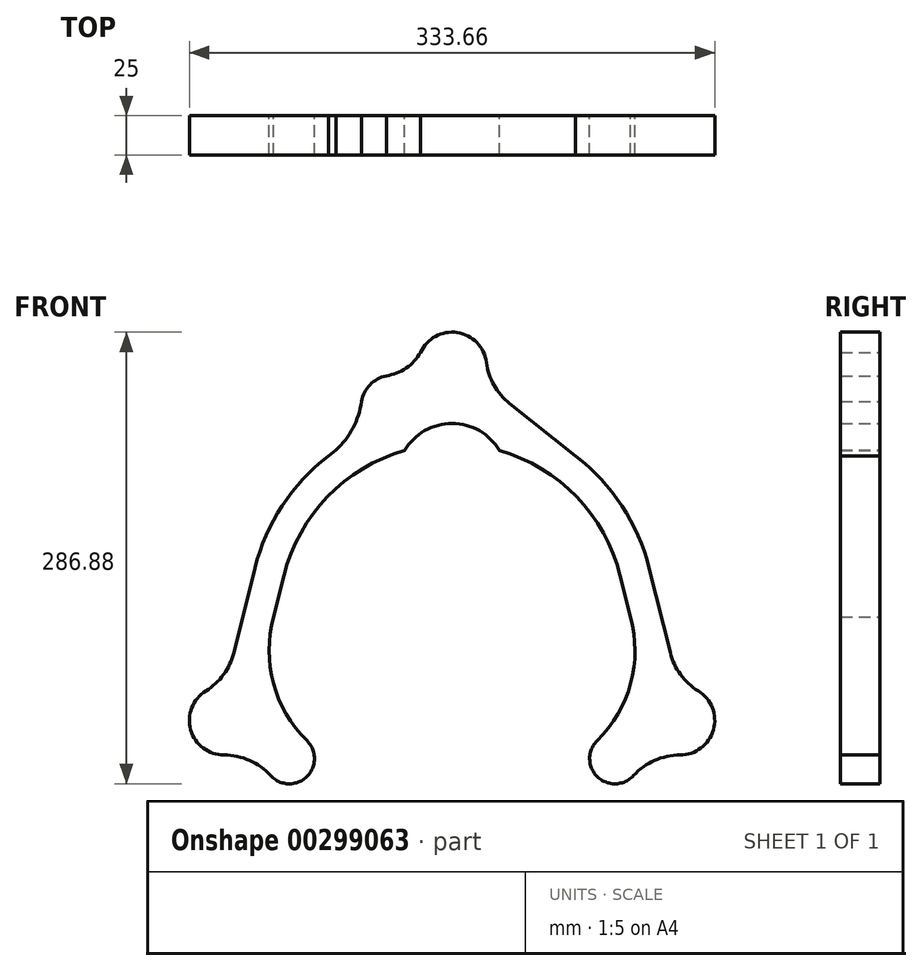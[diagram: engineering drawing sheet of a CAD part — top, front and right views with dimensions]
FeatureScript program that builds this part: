
annotation { "Feature Type Name" : "Feature", "Feature Type Description" : "" }
export const myFeature = defineFeature(function(context is Context, id is Id, definition is map)
    precondition{}
    {
        {
            var Q0;
            Q0=qCreatedBy(makeId("Front.planeOp"),FACE);
            var sketch = newSketch(context, id + "F0", { "sketchPlane" : qUnion([Q0])});
            skPoint(sketch, "E0", {"position": v(0, 88) * mm});
            skArc(sketch, "E1", {"start": v(30.14, 105.79) * mm, "mid": v(17.35, 118.4) * mm, "end": v(0, 123) * mm});
            skLineSegment(sketch, "E2", {"start": v(106.73, 26.61) * mm, "end": v(125.17, 31.2) * mm});
            skLineSegment(sketch, "E3", {"start": v(106.73, 26.61) * mm, "end": v(113.37, 0) * mm});
            skLineSegment(sketch, "E4", {"start": v(113.28, 0) * mm, "end": v(132.95, 0) * mm});
            skArc(sketch, "E5.trimOffspring", {"start": v(106.73, 26.61) * mm, "mid": v(79.06, 76.48) * mm, "end": v(30.14, 105.79) * mm});
            skPoint(sketch, "E6", {"position": v(103.4, -89.88) * mm});
            skArc(sketch, "E7", {"start": v(92.2, -78.45) * mm, "mid": v(92.3, -101.4) * mm, "end": v(115.22, -100.66) * mm});
            skLineSegment(sketch, "E8.trimOffspring", {"start": v(76.29, -181.97) * mm, "end": v(78.18, -189.55) * mm});
            skArc(sketch, "E9.trimOffspring", {"start": v(92.2, -78.45) * mm, "mid": v(113.45, -42.1) * mm, "end": v(113.28, 0) * mm});
            skPoint(sketch, "E10", {"position": v(144.83, -65.62) * mm});
            skArc(sketch, "E11", {"start": v(144.8, -87.62) * mm, "mid": v(166, -71.63) * mm, "end": v(156.38, -46.9) * mm});
            skArc(sketch, "E12.trimOffspring", {"start": v(144.8, -87.62) * mm, "mid": v(128.64, -91.02) * mm, "end": v(115.22, -100.66) * mm});
            skLineSegment(sketch, "E13.0", {"start": v(125.17, 31.2) * mm, "end": v(131.8, 4.6) * mm});
            skLineSegment(sketch, "E14", {"start": v(131.8, 4.6) * mm, "end": v(138.57, -22.53) * mm});
            skArc(sketch, "E15.trimOffspring", {"start": v(138.57, -22.53) * mm, "mid": v(145.09, -36.46) * mm, "end": v(156.38, -46.9) * mm});
            skArc(sketch, "E16.0", {"start": v(125.17, 31.2) * mm, "mid": v(107.88, 70.73) * mm, "end": v(78.53, 102.34) * mm});
            skLineSegment(sketch, "E17", {"start": v(78.53, 102.34) * mm, "end": v(36.58, 135.71) * mm});
            skArc(sketch, "E18", {"start": v(21.82, 161.84) * mm, "mid": v(14.52, 175.53) * mm, "end": v(0, 181) * mm});
            skLineSegment(sketch, "E19.0", {"start": v(103.43, 133.65) * mm, "end": v(102.88, 134.08) * mm});
            skArc(sketch, "E20", {"start": v(21.82, 161.84) * mm, "mid": v(26.65, 147.34) * mm, "end": v(36.58, 135.71) * mm});
            skPoint(sketch, "E21", {"position": v(-37.77, 127.52) * mm});
            skPoint(sketch, "E22", {"position": v(-37.77, 133.59) * mm});
            skArc(sketch, "E23", {"start": v(-41.75, 153.26) * mm, "mid": v(-52.18, 147.56) * mm, "end": v(-57.55, 136.96) * mm});
            skLineSegment(sketch, "E24.MirrorCS", {"start": v(-103.43, 133.65) * mm, "end": v(-102.88, 134.08) * mm});
            skLineSegment(sketch, "E25.MirrorCS", {"start": v(-78.53, 102.34) * mm, "end": v(-69.5, 109.52) * mm});
            skArc(sketch, "E26.MirrorCS", {"start": v(-144.8, -87.62) * mm, "mid": v(-166, -71.63) * mm, "end": v(-156.38, -46.9) * mm});
            skArc(sketch, "E27.MirrorCS", {"start": v(-92.2, -78.45) * mm, "mid": v(-92.3, -101.4) * mm, "end": v(-115.22, -100.66) * mm});
            skArc(sketch, "E28.MirrorCS", {"start": v(-138.57, -22.53) * mm, "mid": v(-145.09, -36.46) * mm, "end": v(-156.38, -46.9) * mm});
            skArc(sketch, "E29.MirrorCS", {"start": v(-144.8, -87.62) * mm, "mid": v(-128.64, -91.02) * mm, "end": v(-115.22, -100.66) * mm});
            skArc(sketch, "E30.MirrorCS", {"start": v(-125.17, 31.2) * mm, "mid": v(-107.88, 70.73) * mm, "end": v(-78.53, 102.34) * mm});
            skArc(sketch, "E31.MirrorCS", {"start": v(-20, 168.15) * mm, "mid": v(-11.89, 177.51) * mm, "end": v(0, 181) * mm});
            skLineSegment(sketch, "E32.MirrorCS", {"start": v(-125.17, 31.2) * mm, "end": v(-131.8, 4.6) * mm});
            skLineSegment(sketch, "E33.MirrorCS", {"start": v(-113.28, 0) * mm, "end": v(-132.95, 0) * mm});
            skLineSegment(sketch, "E34.MirrorCS", {"start": v(-106.73, 26.61) * mm, "end": v(-113.37, 0) * mm});
            skArc(sketch, "E35.MirrorCS", {"start": v(-106.73, 26.61) * mm, "mid": v(-79.06, 76.48) * mm, "end": v(-30.14, 105.79) * mm});
            skArc(sketch, "E36.MirrorCS", {"start": v(-30.14, 105.79) * mm, "mid": v(-17.35, 118.4) * mm, "end": v(0, 123) * mm});
            skArc(sketch, "E37.MirrorCS", {"start": v(-92.2, -78.45) * mm, "mid": v(-113.45, -42.1) * mm, "end": v(-113.28, 0) * mm});
            skLineSegment(sketch, "E38.MirrorCS", {"start": v(-131.8, 4.6) * mm, "end": v(-138.57, -22.53) * mm});
            skPoint(sketch, "E39.orphan", {"position": v(-21.82, 161.84) * mm});
            skArc(sketch, "E40.trimOffspring", {"start": v(-41.75, 153.26) * mm, "mid": v(-29.15, 158.2) * mm, "end": v(-20, 168.15) * mm});
            skPoint(sketch, "E41.orphan", {"position": v(-36.58, 135.71) * mm});
            skArc(sketch, "E42.trimOffspring", {"start": v(-78.5, 102.36) * mm, "mid": v(-64.4, 117.47) * mm, "end": v(-57.55, 136.96) * mm});
            skPoint(sketch, "E43.orphan", {"position": v(-162.87, 40.6) * mm});
            skPoint(sketch, "E44.orphan", {"position": v(-164.51, 0) * mm});
            skPoint(sketch, "E45.orphan", {"position": v(164.51, 0) * mm});
            skPoint(sketch, "E46.orphan", {"position": v(162.87, 40.6) * mm});
            skLineSegment(sketch, "E47.trimOffspring", {"start": v(0, 123) * mm, "end": v(0, 191.24) * mm});
            skSolve(sketch);
        }
        {
            var Q0;
            Q0 = qSketchRegion(id + "F0", true);
            extrude(context, id + "F1", {"entities" : qUnion([Q0]), "depth" : 25 * mm});
        }
    });
